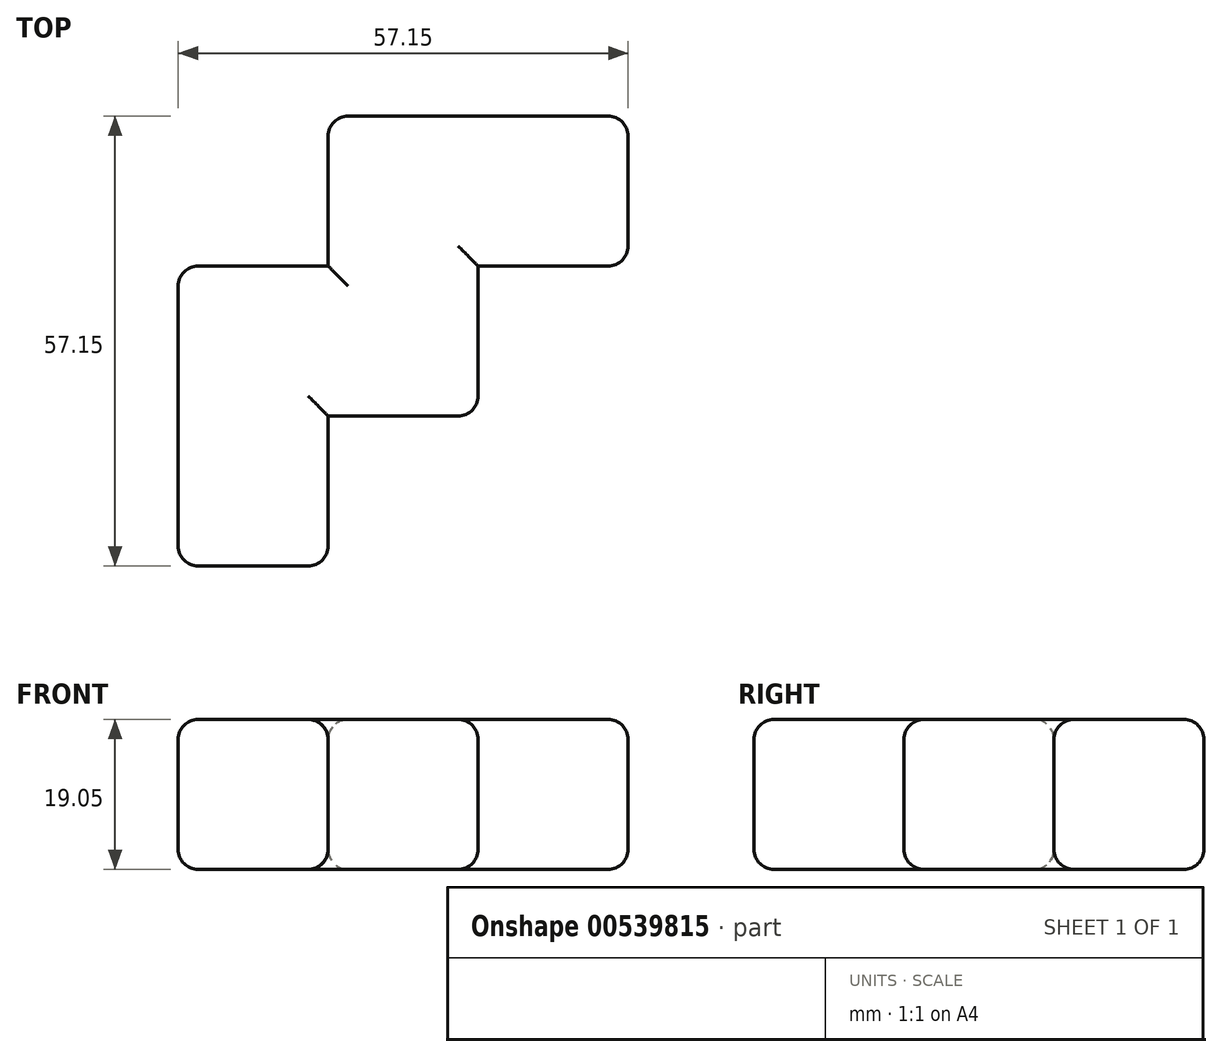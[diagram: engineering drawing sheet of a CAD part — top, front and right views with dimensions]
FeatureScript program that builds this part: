
annotation { "Feature Type Name" : "Feature", "Feature Type Description" : "" }
export const myFeature = defineFeature(function(context is Context, id is Id, definition is map)
    precondition{}
    {
        {
            var Q0;
            Q0=qCreatedBy(makeId("Top.planeOp"),FACE);
            var sketch = newSketch(context, id + "F0", { "sketchPlane" : qUnion([Q0])});
            skLineSegment(sketch, "E0", {"start": v(0, 38.1) * mm, "end": v(19.05, 38.1) * mm});
            skLineSegment(sketch, "E1", {"start": v(19.05, 38.1) * mm, "end": v(19.05, 57.15) * mm});
            skLineSegment(sketch, "E2", {"start": v(19.05, 57.15) * mm, "end": v(57.15, 57.15) * mm});
            skLineSegment(sketch, "E3", {"start": v(57.15, 57.15) * mm, "end": v(57.15, 38.1) * mm});
            skLineSegment(sketch, "E4", {"start": v(57.15, 38.1) * mm, "end": v(38.1, 38.1) * mm});
            skLineSegment(sketch, "E5", {"start": v(38.1, 38.1) * mm, "end": v(38.1, 19.05) * mm});
            skLineSegment(sketch, "E6", {"start": v(38.1, 19.05) * mm, "end": v(19.05, 19.05) * mm});
            skLineSegment(sketch, "E7", {"start": v(19.05, 19.05) * mm, "end": v(19.05, 0) * mm});
            skLineSegment(sketch, "E8", {"start": v(19.05, 0) * mm, "end": v(0, 0) * mm});
            skLineSegment(sketch, "E9", {"start": v(0, 0) * mm, "end": v(0, 38.1) * mm});
            skSolve(sketch);
        }
        {
            var Q0;
            Q0=makeQuery(id+"F0.imprint","IMPRINT",FACE,{"disambiguationData":[TD([[makeQuery(id+"F0.imprint","IMPRINT",EDGE,{"derivedFrom":sQuery(id+"F0.wireOp",EDGE,"E0")}),-1.0]])]});
            extrude(context, id + "F1", {"entities" : qUnion([Q0]), "depth" : 19.05 * mm, "offsetDistance" : 25.4 * mm});
        }
        {
            var Q0;
            Q0=makeQuery(id+"F1.opExtrude","CAP_FACE",FACE,{"disambiguationData":[OSD([sQuery(id+"F0.wireOp",EDGE,"E0"),sQuery(id+"F0.wireOp",EDGE,"E1"),sQuery(id+"F0.wireOp",EDGE,"E2"),sQuery(id+"F0.wireOp",EDGE,"E3"),sQuery(id+"F0.wireOp",EDGE,"E4"),sQuery(id+"F0.wireOp",EDGE,"E5"),sQuery(id+"F0.wireOp",EDGE,"E6"),sQuery(id+"F0.wireOp",EDGE,"E7"),sQuery(id+"F0.wireOp",EDGE,"E8"),sQuery(id+"F0.wireOp",EDGE,"E9")])],"isStart":false});
            var Q1;
            Q1=makeQuery(id+"F1.opExtrude","CAP_FACE",FACE,{"disambiguationData":[OSD([sQuery(id+"F0.wireOp",EDGE,"E0"),sQuery(id+"F0.wireOp",EDGE,"E1"),sQuery(id+"F0.wireOp",EDGE,"E2"),sQuery(id+"F0.wireOp",EDGE,"E3"),sQuery(id+"F0.wireOp",EDGE,"E4"),sQuery(id+"F0.wireOp",EDGE,"E5"),sQuery(id+"F0.wireOp",EDGE,"E6"),sQuery(id+"F0.wireOp",EDGE,"E7"),sQuery(id+"F0.wireOp",EDGE,"E8"),sQuery(id+"F0.wireOp",EDGE,"E9")])],"isStart":true});
            var Q2;
            Q2=makeQuery(id+"F1.opExtrude","SWEPT_FACE",FACE,{"disambiguationData":[OSD([sQuery(id+"F0.wireOp",EDGE,"E8")])]});
            var Q3;
            Q3=makeQuery(id+"F1.opExtrude","SWEPT_FACE",FACE,{"disambiguationData":[OSD([sQuery(id+"F0.wireOp",EDGE,"E3")])]});
            var Q4;
            Q4=makeQuery(id+"F1.opExtrude","SWEPT_EDGE",EDGE,{"disambiguationData":[OSD([sQuery(id+"F0.wireOp",EDGE,"E5"),sQuery(id+"F0.wireOp",EDGE,"E6")])]});
            var Q5;
            Q5=makeQuery(id+"F1.opExtrude","SWEPT_EDGE",EDGE,{"disambiguationData":[OSD([sQuery(id+"F0.wireOp",EDGE,"E1"),sQuery(id+"F0.wireOp",EDGE,"E2")])]});
            var Q6;
            Q6=makeQuery(id+"F1.opExtrude","SWEPT_EDGE",EDGE,{"disambiguationData":[OSD([sQuery(id+"F0.wireOp",EDGE,"E0"),sQuery(id+"F0.wireOp",EDGE,"E9")])]});
            fillet(context, id + "F2", {"entities" : qUnion([Q0, Q1, Q2, Q3, Q4, Q5, Q6]), "radius" : 2.54 * mm, "tangentPropagation" : true, "allowEdgeOverflow" : false});
        }
    });
